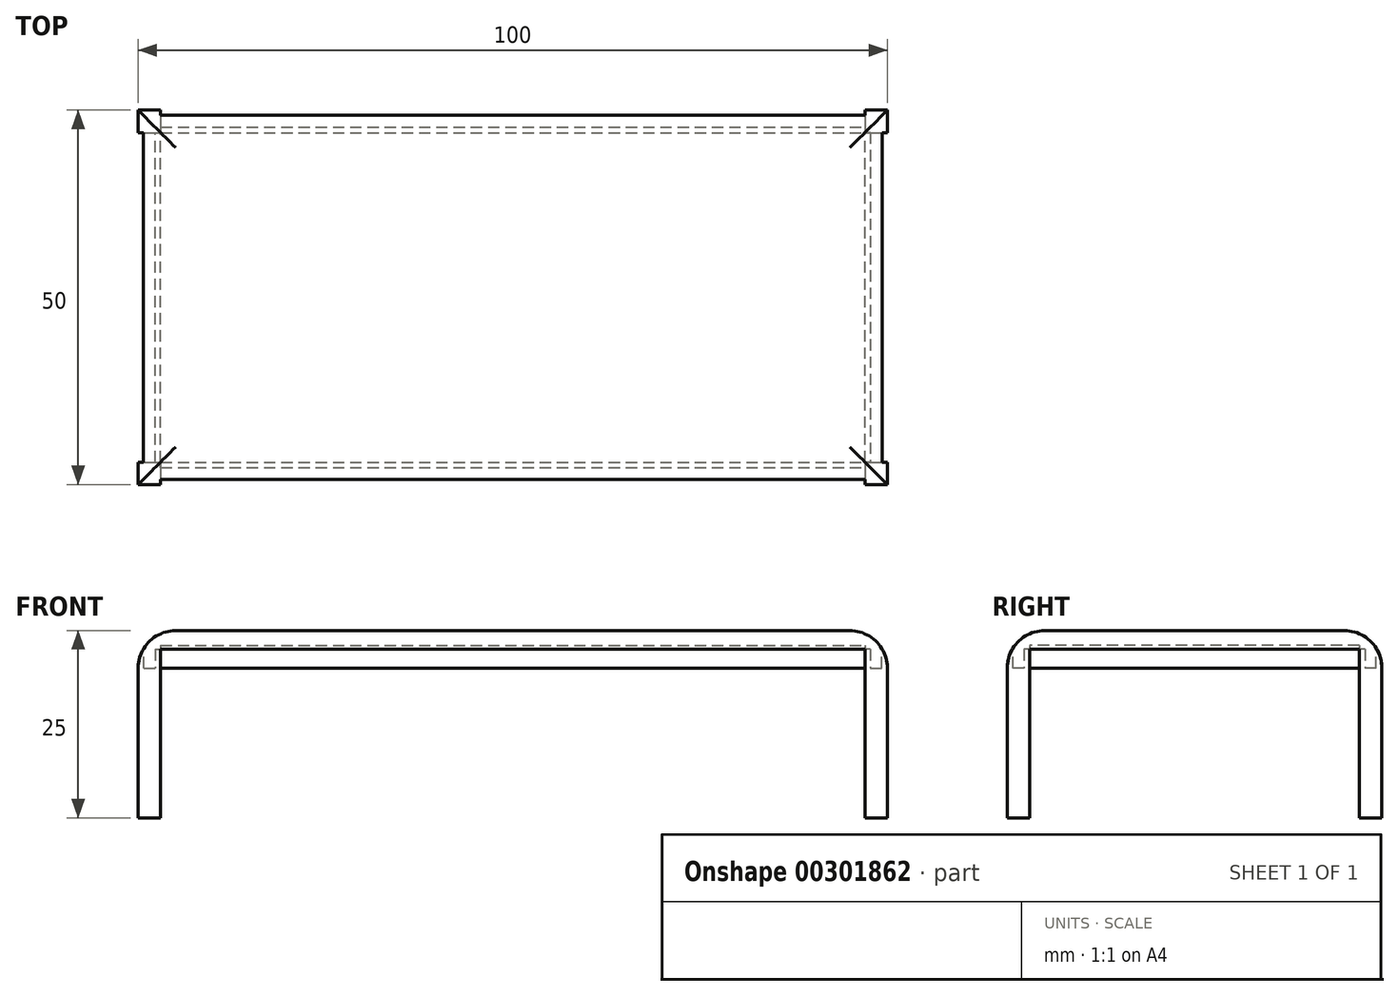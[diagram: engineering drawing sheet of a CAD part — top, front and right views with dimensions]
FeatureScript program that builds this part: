
annotation { "Feature Type Name" : "Feature", "Feature Type Description" : "" }
export const myFeature = defineFeature(function(context is Context, id is Id, definition is map)
    precondition{}
    {
        {
            var Q0;
            Q0=qCreatedBy(makeId("Top.planeOp"),FACE);
            var sketch = newSketch(context, id + "F0", { "sketchPlane" : qUnion([Q0])});
            skLineSegment(sketch, "E0.bottom", {"start": v(0, 0) * mm, "end": v(100, 0) * mm});
            skLineSegment(sketch, "E0.top", {"start": v(0, 50) * mm, "end": v(100, 50) * mm});
            skLineSegment(sketch, "E0.left", {"start": v(0, 0) * mm, "end": v(0, 50) * mm});
            skLineSegment(sketch, "E0.right", {"start": v(100, 0) * mm, "end": v(100, 50) * mm});
            skSolve(sketch);
        }
        {
            var Q0;
            Q0 = qSketchRegion(id + "F0", true);
            extrude(context, id + "F1", {"entities" : qUnion([Q0]), "depth" : 25 * mm});
        }
        {
            var Q0;
            Q0=makeQuery(id+"F1.opExtrude","SWEPT_FACE",FACE,{"disambiguationData":[OSD([sQuery(id+"F0.wireOp",EDGE,"E0.bottom")])]});
            var sketch = newSketch(context, id + "F2", { "sketchPlane" : qUnion([Q0])});
            skLineSegment(sketch, "E1", {"start": v(0, 0) * mm, "end": v(3, 0) * mm});
            skLineSegment(sketch, "E2", {"start": v(3, 0) * mm, "end": v(3, 20) * mm});
            skLineSegment(sketch, "E3", {"start": v(100, 0) * mm, "end": v(97, 0) * mm});
            skLineSegment(sketch, "E4", {"start": v(97, 0) * mm, "end": v(97, 20) * mm});
            skLineSegment(sketch, "E5", {"start": v(3, 20) * mm, "end": v(97, 20) * mm});
            skLineSegment(sketch, "E6", {"start": v(3, 20) * mm, "end": v(3, 22.5) * mm});
            skLineSegment(sketch, "E7", {"start": v(97, 20) * mm, "end": v(97, 22.5) * mm});
            skLineSegment(sketch, "E8", {"start": v(3, 22.5) * mm, "end": v(97, 22.5) * mm});
            skSolve(sketch);
        }
        {
            var Q0;
            Q0=makeQuery(id+"F1.opExtrude","SWEPT_FACE",FACE,{"disambiguationData":[OSD([sQuery(id+"F0.wireOp",EDGE,"E0.right")])]});
            var sketch = newSketch(context, id + "F3", { "sketchPlane" : qUnion([Q0])});
            skLineSegment(sketch, "E9", {"start": v(0, 0) * mm, "end": v(3, 0) * mm});
            skLineSegment(sketch, "E10", {"start": v(3, 0) * mm, "end": v(3, 20) * mm});
            skLineSegment(sketch, "E11", {"start": v(50, 0) * mm, "end": v(47, 0) * mm});
            skLineSegment(sketch, "E12", {"start": v(47, 0) * mm, "end": v(47, 20) * mm});
            skLineSegment(sketch, "E13", {"start": v(3, 20) * mm, "end": v(47, 20) * mm});
            skSolve(sketch);
        }
        {
            var Q0;
            {var subQ0=sQuery(id+"F3.wireOp",EDGE,"E10");Q0=makeQuery(id+"F3.imprint","IMPRINT",FACE,{"disambiguationData":[TD([[makeQuery(id+"F3.imprint","IMPRINT",EDGE,{"derivedFrom":subQ0}),-1.0]])]});}
            extrude(context, id + "F4", {"entities" : qUnion([Q0]), "operationType" : NewBodyOperationType.REMOVE, "endBound" : BoundingType.THROUGH_ALL, "oppositeDirection" : true, "depth" : 25 * mm});
        }
        {
            var Q0;
            {var subQ0=sQuery(id+"F2.wireOp",EDGE,"E2");Q0=makeQuery(id+"F2.imprint","IMPRINT",FACE,{"disambiguationData":[TD([[makeQuery(id+"F2.imprint","IMPRINT",EDGE,{"derivedFrom":subQ0}),-1.0]])]});}
            extrude(context, id + "F5", {"entities" : qUnion([Q0]), "operationType" : NewBodyOperationType.REMOVE, "endBound" : BoundingType.THROUGH_ALL, "oppositeDirection" : true, "depth" : 25 * mm});
        }
        {
            var Q0;
            Q0=makeQuery(id+"F5.boolean.opBoolean","MERGE",FACE,{"derivedFrom":[makeQuery(id+"F4.boolean.opBoolean","COPY",FACE,{"derivedFrom":makeQuery(id+"F4.opExtrude","SWEPT_FACE",FACE,{"disambiguationData":[OSD([sQuery(id+"F3.wireOp",EDGE,"E13")])]})}),makeQuery(id+"F5.opExtrude","SWEPT_FACE",FACE,{"disambiguationData":[OSD([sQuery(id+"F2.wireOp",EDGE,"E5")])]})]});
            var sketch = newSketch(context, id + "F6", { "sketchPlane" : qUnion([Q0])});
            skLineSegment(sketch, "E14", {"start": v(3, -3) * mm, "end": v(3, -47) * mm});
            skLineSegment(sketch, "E15", {"start": v(3, -47) * mm, "end": v(97, -47) * mm});
            skLineSegment(sketch, "E16", {"start": v(97, -47) * mm, "end": v(97, -3) * mm});
            skLineSegment(sketch, "E17", {"start": v(3, -3) * mm, "end": v(97, -3) * mm});
            skLineSegment(sketch, "E18", {"start": v(3, -1.5) * mm, "end": v(3, -0.75) * mm});
            skLineSegment(sketch, "E19", {"start": v(3, -0.75) * mm, "end": v(3, -1.5) * mm});
            skLineSegment(sketch, "E20", {"start": v(3, -1.5) * mm, "end": v(3, -2.25) * mm});
            skLineSegment(sketch, "E21", {"start": v(3, -2.25) * mm, "end": v(97, -2.25) * mm});
            skLineSegment(sketch, "E22", {"start": v(3, -0.75) * mm, "end": v(97, -0.75) * mm});
            skSolve(sketch);
        }
        {
            var Q0;
            Q0=makeQuery(id+"F6.imprint","IMPRINT",FACE,{"disambiguationData":[TD([[makeQuery(id+"F6.imprint","IMPRINT",EDGE,{"derivedFrom":sQuery(id+"F6.wireOp",EDGE,"E14")}),1.0]])]});
            var Q1;
            {var subQ0=sQuery(id+"F6.wireOp",EDGE,"E17");Q1=makeQuery(id+"F6.imprint","IMPRINT",FACE,{"disambiguationData":[TD([[makeQuery(id+"F6.imprint","IMPRINT",EDGE,{"derivedFrom":subQ0}),1.0]])]});}
            extrude(context, id + "F7", {"entities" : qUnion([Q0, Q1]), "operationType" : NewBodyOperationType.REMOVE, "oppositeDirection" : true, "depth" : 2.5 * mm});
        }
        {
            var Q0;
            Q0 = qSketchRegion(id + "F6", true);
            extrude(context, id + "F8", {"entities" : qUnion([Q0]), "operationType" : NewBodyOperationType.REMOVE, "oppositeDirection" : true, "depth" : 3 * mm});
        }
        {
            var Q0;
            Q0 = qSketchRegion(id + "F2", true);
            extrude(context, id + "F9", {"entities" : qUnion([Q0]), "operationType" : NewBodyOperationType.REMOVE, "oppositeDirection" : true, "depth" : .75 * mm});
        }
        {
            var Q0;
            Q0=makeQuery(id+"F1.opExtrude","SWEPT_FACE",FACE,{"disambiguationData":[OSD([sQuery(id+"F0.wireOp",EDGE,"E0.left")])]});
            var sketch = newSketch(context, id + "F10", { "sketchPlane" : qUnion([Q0])});
            skLineSegment(sketch, "E23", {"start": v(-47, 20) * mm, "end": v(-47, 22.5) * mm});
            skLineSegment(sketch, "E24", {"start": v(-3, 20) * mm, "end": v(-3, 22.5) * mm});
            skLineSegment(sketch, "E25", {"start": v(-47, 22.5) * mm, "end": v(-3, 22.5) * mm});
            skSolve(sketch);
        }
        {
            var Q0;
            Q0=makeQuery(id+"F10.imprint","IMPRINT",FACE,{"disambiguationData":[TD([[makeQuery(id+"F10.imprint","IMPRINT",EDGE,{"derivedFrom":sQuery(id+"F10.wireOp",EDGE,"E23")}),-1.0]])]});
            extrude(context, id + "F11", {"entities" : qUnion([Q0]), "operationType" : NewBodyOperationType.REMOVE, "oppositeDirection" : true, "depth" : .75 * mm});
        }
        {
            var Q0;
            {var subQ0=sQuery(id+"F2.wireOp",EDGE,"E6");var subQ1=sQuery(id+"F6.wireOp",EDGE,"E14");var subQ2=sQuery(id+"F2.wireOp",EDGE,"E5");var subQ3=sQuery(id+"F2.wireOp",EDGE,"E2");var subQ4=sQuery(id+"F0.wireOp",EDGE,"E0.bottom");Q0=makeQuery(id+"F9.boolean.opBoolean","MERGE",FACE,{"derivedFrom":[makeQuery(id+"F8.boolean.opBoolean","MERGE",FACE,{"derivedFrom":[makeQuery(id+"F7.boolean.opBoolean","MERGE",FACE,{"derivedFrom":[makeQuery(id+"F5.boolean.opBoolean","COPY",FACE,{"disambiguationData":[TD([makeQuery(id+"F1.opExtrude","SWEPT_FACE",FACE,{"disambiguationData":[OSD([subQ4])]})])],"derivedFrom":makeQuery(id+"F5.opExtrude","SWEPT_FACE",FACE,{"disambiguationData":[OSD([subQ3])]})}),makeQuery(id+"F7.opExtrude","SWEPT_FACE",FACE,{"disambiguationData":[OSD([subQ3,subQ2,subQ0,subQ1])]})]}),makeQuery(id+"F8.opExtrude","SWEPT_FACE",FACE,{"disambiguationData":[OSD([subQ1])]})]}),makeQuery(id+"F9.opExtrude","SWEPT_FACE",FACE,{"disambiguationData":[OSD([subQ0])]})]});}
            var sketch = newSketch(context, id + "F12", { "sketchPlane" : qUnion([Q0])});
            skLineSegment(sketch, "E26", {"start": v(3, 20) * mm, "end": v(3, 22.5) * mm});
            skLineSegment(sketch, "E27", {"start": v(47, 20) * mm, "end": v(47, 21.5) * mm});
            skLineSegment(sketch, "E28", {"start": v(3, 22.5) * mm, "end": v(47, 22.5) * mm});
            skSolve(sketch);
        }
        {
            var Q0;
            Q0=makeQuery(id+"F12.imprint","IMPRINT",FACE,{"disambiguationData":[TD([[makeQuery(id+"F12.imprint","IMPRINT",EDGE,{"derivedFrom":sQuery(id+"F12.wireOp",EDGE,"E26")}),-1.0]])]});
            extrude(context, id + "F13", {"entities" : qUnion([Q0]), "operationType" : NewBodyOperationType.REMOVE, "oppositeDirection" : true, "depth" : .75 * mm});
        }
        {
            var Q0;
            Q0=makeQuery(id+"F1.opExtrude","SWEPT_FACE",FACE,{"disambiguationData":[OSD([sQuery(id+"F0.wireOp",EDGE,"E0.right")])]});
            var sketch = newSketch(context, id + "F14", { "sketchPlane" : qUnion([Q0])});
            skLineSegment(sketch, "E29", {"start": v(3, 20) * mm, "end": v(3, 22.5) * mm});
            skLineSegment(sketch, "E30", {"start": v(47, 20) * mm, "end": v(47, 22.5) * mm});
            skLineSegment(sketch, "E31", {"start": v(3, 22.5) * mm, "end": v(47, 22.5) * mm});
            skSolve(sketch);
        }
        {
            var Q0;
            Q0=makeQuery(id+"F14.imprint","IMPRINT",FACE,{"disambiguationData":[TD([[makeQuery(id+"F14.imprint","IMPRINT",EDGE,{"derivedFrom":sQuery(id+"F14.wireOp",EDGE,"E29")}),-1.0]])]});
            extrude(context, id + "F15", {"entities" : qUnion([Q0]), "operationType" : NewBodyOperationType.REMOVE, "oppositeDirection" : true, "depth" : .75 * mm});
        }
        {
            var Q0;
            {var subQ0=sQuery(id+"F2.wireOp",EDGE,"E7");var subQ1=sQuery(id+"F6.wireOp",EDGE,"E16");var subQ2=sQuery(id+"F2.wireOp",EDGE,"E5");var subQ3=sQuery(id+"F2.wireOp",EDGE,"E4");var subQ4=sQuery(id+"F0.wireOp",EDGE,"E0.bottom");Q0=makeQuery(id+"F9.boolean.opBoolean","MERGE",FACE,{"derivedFrom":[makeQuery(id+"F8.boolean.opBoolean","MERGE",FACE,{"derivedFrom":[makeQuery(id+"F7.boolean.opBoolean","MERGE",FACE,{"derivedFrom":[makeQuery(id+"F5.boolean.opBoolean","COPY",FACE,{"disambiguationData":[TD([makeQuery(id+"F1.opExtrude","SWEPT_FACE",FACE,{"disambiguationData":[OSD([subQ4])]})])],"derivedFrom":makeQuery(id+"F5.opExtrude","SWEPT_FACE",FACE,{"disambiguationData":[OSD([subQ3])]})}),makeQuery(id+"F7.opExtrude","SWEPT_FACE",FACE,{"disambiguationData":[OSD([subQ3,subQ2,subQ0,subQ1])]})]}),makeQuery(id+"F8.opExtrude","SWEPT_FACE",FACE,{"disambiguationData":[OSD([subQ1])]})]}),makeQuery(id+"F9.opExtrude","SWEPT_FACE",FACE,{"disambiguationData":[OSD([subQ0])]})]});}
            var sketch = newSketch(context, id + "F16", { "sketchPlane" : qUnion([Q0])});
            skLineSegment(sketch, "E32", {"start": v(-3, 20) * mm, "end": v(-3, 22.5) * mm});
            skLineSegment(sketch, "E33", {"start": v(-3, 22.5) * mm, "end": v(-47, 22.5) * mm});
            skPoint(sketch, "E33.endSnap0", {"position": v(-47, 21.5) * mm});
            skLineSegment(sketch, "E34", {"start": v(-47, 22.5) * mm, "end": v(-47, 20) * mm});
            skSolve(sketch);
        }
        {
            var Q0;
            Q0=makeQuery(id+"F16.imprint","IMPRINT",FACE,{"disambiguationData":[TD([[makeQuery(id+"F16.imprint","IMPRINT",EDGE,{"derivedFrom":sQuery(id+"F16.wireOp",EDGE,"E32")}),1.0]])]});
            extrude(context, id + "F17", {"entities" : qUnion([Q0]), "operationType" : NewBodyOperationType.REMOVE, "oppositeDirection" : true, "depth" : .75 * mm});
        }
        {
            var Q0;
            Q0=makeQuery(id+"F1.opExtrude","SWEPT_FACE",FACE,{"disambiguationData":[OSD([sQuery(id+"F0.wireOp",EDGE,"E0.top")])]});
            var sketch = newSketch(context, id + "F18", { "sketchPlane" : qUnion([Q0])});
            skLineSegment(sketch, "E35", {"start": v(-97, 20) * mm, "end": v(-97, 22.5) * mm});
            skLineSegment(sketch, "E36", {"start": v(-3, 20) * mm, "end": v(-3, 22.5) * mm});
            skLineSegment(sketch, "E37", {"start": v(-97, 22.5) * mm, "end": v(-3, 22.5) * mm});
            skSolve(sketch);
        }
        {
            var Q0;
            Q0=makeQuery(id+"F18.imprint","IMPRINT",FACE,{"disambiguationData":[TD([[makeQuery(id+"F18.imprint","IMPRINT",EDGE,{"derivedFrom":sQuery(id+"F18.wireOp",EDGE,"E35")}),-1.0]])]});
            extrude(context, id + "F19", {"entities" : qUnion([Q0]), "operationType" : NewBodyOperationType.REMOVE, "oppositeDirection" : true, "depth" : .75 * mm});
        }
        {
            var Q0;
            {var subQ0=sQuery(id+"F3.wireOp",EDGE,"E13");var subQ2=sQuery(id+"F0.wireOp",EDGE,"E0.right");var subQ3=sQuery(id+"F0.wireOp",EDGE,"E0.left");var subQ5=sQuery(id+"F2.wireOp",EDGE,"E5");var subQ7=sQuery(id+"F3.wireOp",EDGE,"E12");var subQ8=makeQuery(id+"F4.boolean.opBoolean","COPY",FACE,{"derivedFrom":makeQuery(id+"F4.opExtrude","SWEPT_FACE",FACE,{"disambiguationData":[OSD([subQ7])]})});var subQ9=sQuery(id+"F6.wireOp",EDGE,"E15");var subQ10=sQuery(id+"F2.wireOp",EDGE,"E2");Q0=makeQuery(id+"F17.boolean.opBoolean","MERGE",FACE,{"derivedFrom":[makeQuery(id+"F13.boolean.opBoolean","MERGE",FACE,{"derivedFrom":[makeQuery(id+"F8.boolean.opBoolean","MERGE",FACE,{"derivedFrom":[makeQuery(id+"F7.boolean.opBoolean","COPY",FACE,{"derivedFrom":makeQuery(id+"F7.opExtrude","SWEPT_FACE",FACE,{"disambiguationData":[OSD([subQ9])]})}),makeQuery(id+"F8.opExtrude","SWEPT_FACE",FACE,{"disambiguationData":[OSD([subQ9])]})]}),makeQuery(id+"F11.boolean.opBoolean","MERGE",FACE,{"derivedFrom":[makeQuery(id+"F5.boolean.opBoolean","SPLIT",FACE,{"disambiguationData":[TD([makeQuery(id+"F1.opExtrude","SWEPT_FACE",FACE,{"disambiguationData":[OSD([subQ3])]})])],"derivedFrom":subQ8}),makeQuery(id+"F11.opExtrude","SWEPT_FACE",FACE,{"disambiguationData":[OSD([sQuery(id+"F10.wireOp",EDGE,"E23")])]})]}),makeQuery(id+"F13.opExtrude","SWEPT_FACE",FACE,{"disambiguationData":[OSD([subQ10,subQ5,sQuery(id+"F2.wireOp",EDGE,"E6"),subQ7,subQ0,sQuery(id+"F6.wireOp",EDGE,"E14"),subQ9,sQuery(id+"F12.wireOp",EDGE,"E27")])]})]}),makeQuery(id+"F15.boolean.opBoolean","MERGE",FACE,{"derivedFrom":[makeQuery(id+"F5.boolean.opBoolean","SPLIT",FACE,{"disambiguationData":[TD([makeQuery(id+"F1.opExtrude","SWEPT_FACE",FACE,{"disambiguationData":[OSD([subQ2])]})])],"derivedFrom":subQ8}),makeQuery(id+"F15.opExtrude","SWEPT_FACE",FACE,{"disambiguationData":[OSD([sQuery(id+"F14.wireOp",EDGE,"E30")])]})]}),makeQuery(id+"F17.opExtrude","SWEPT_FACE",FACE,{"disambiguationData":[OSD([sQuery(id+"F16.wireOp",EDGE,"E34")])]})]});}
            var sketch = newSketch(context, id + "F20", { "sketchPlane" : qUnion([Q0])});
            skLineSegment(sketch, "E38", {"start": v(3, 20) * mm, "end": v(3, 22.5) * mm});
            skLineSegment(sketch, "E39", {"start": v(3, 22.5) * mm, "end": v(97, 22.5) * mm});
            skLineSegment(sketch, "E40", {"start": v(97, 22.5) * mm, "end": v(97, 20) * mm});
            skSolve(sketch);
        }
        {
            var Q0;
            Q0=makeQuery(id+"F20.imprint","IMPRINT",FACE,{"disambiguationData":[TD([[makeQuery(id+"F20.imprint","IMPRINT",EDGE,{"derivedFrom":sQuery(id+"F20.wireOp",EDGE,"E38")}),-1.0]])]});
            extrude(context, id + "F21", {"entities" : qUnion([Q0]), "operationType" : NewBodyOperationType.REMOVE, "oppositeDirection" : true, "depth" : .75 * mm});
        }
        {
            var Q0;
            Q0=makeQuery(id+"F1.opExtrude","CAP_FACE",FACE,{"disambiguationData":[OSD([sQuery(id+"F0.wireOp",EDGE,"E0.bottom"),sQuery(id+"F0.wireOp",EDGE,"E0.top"),sQuery(id+"F0.wireOp",EDGE,"E0.left"),sQuery(id+"F0.wireOp",EDGE,"E0.right")])],"isStart":false});
            fillet(context, id + "F22", {"entities" : qUnion([Q0]), "radius" : 5 * mm, "tangentPropagation" : true, "allowEdgeOverflow" : false});
        }
    });
